# Revit family: EDFPBVM117FPK
name_source: partatom
category: Plumbing Fixtures
units: mm (PartAtom-declared; Revit-internal decimal feet)

## family parameters
Always vertical = Yes
Cut with Voids When Loaded = No
OmniClass Number = 23.45.00.00
OmniClass Title = Sanitary, Laundry, and Cleaning Equipment
Part Type = Normal
Room Calculation Point = No
Round Connector Dimension = Use Radius
Shared = No
Work Plane-Based = No

## types (2) — shared parameters
Activation by = Mechanical Front bubbler Button
Approx. Shipping Weight = 72 lbs
Body Material = Metal - Steel - Stainless - Chrome
Bubbler Style = Vandal Resistant
CW Connection = Yes
Chilling Option = Non-refrigerated
Date = 09-10-2020
Description = Elkay SwirlFlo Bi-Level Fountain Non-Filtered Non-Refrigerated Freeze Resistant Stainless
Dimensions (L x W x H) = 38 1/2 inch x 19 inch x 21 15/16 inch
Finish = Stainless Steel
HW Connection = No
Installation Location = Indoor + Outdoor
Manufacturer = Elkay
Model = EDFPBVM117FPK
Mounting Type = Wall Mount (On Wall)
Number of Stations = 2
Power = No Electrical Required
Sanitary Connector Description = Sanitary Connection
Sanitary Service Size Radius = 22 mm  [stored 0.0721785 ft]
Special Features = Freeze Resistant
URL = https://www.elkay.com
Vent Connection = No
Version = 1.0.0.0
Wall Plate Material = Metal - Steel - Stainless - Chrome
Waste Connection = Yes
Water Connector Description = Water Supply
Water Out Connection Description = Water Return
Water Service Flow = 0 GPM
Water Service Flow Out = 0 GPM
Water Service Size Radius = 11 mm  [stored 0.0360892 ft]

## type names (no varying parameters)
- EDFPBVM117FPK
- EDFPBMV117C

note: [stored X ft] marks values corroborated as IEEE doubles in the binary element streams (Revit-internal decimal feet)

## geometry (parser evidence)
native form markers: Sweep x22
no freeform markers — native parametric forms only
